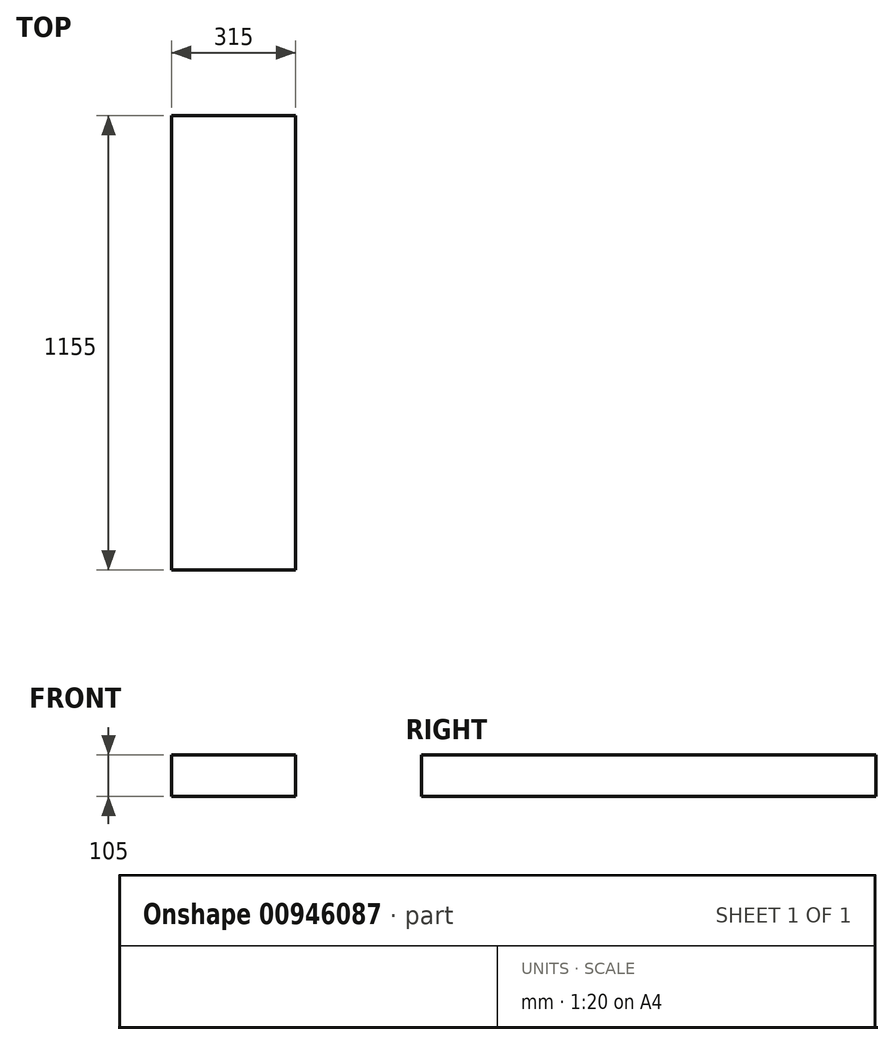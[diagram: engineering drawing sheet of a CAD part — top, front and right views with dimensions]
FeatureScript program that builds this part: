
annotation { "Feature Type Name" : "Feature", "Feature Type Description" : "" }
export const myFeature = defineFeature(function(context is Context, id is Id, definition is map)
    precondition{}
    {
        {
            var Q0;
            Q0=qCreatedBy(makeId("Top.planeOp"),FACE);
            var sketch = newSketch(context, id + "F0", { "sketchPlane" : qUnion([Q0])});
            skLineSegment(sketch, "E0.bottom", {"start": v(-283.8, 1138.94) * mm, "end": v(31.2, 1138.94) * mm});
            skLineSegment(sketch, "E0.top", {"start": v(-283.8, -16.06) * mm, "end": v(31.2, -16.06) * mm});
            skLineSegment(sketch, "E0.left", {"start": v(-283.8, 1138.94) * mm, "end": v(-283.8, -16.06) * mm});
            skLineSegment(sketch, "E0.right", {"start": v(31.2, 1138.94) * mm, "end": v(31.2, -16.06) * mm});
            skSolve(sketch);
        }
        {
            var Q0;
            Q0=qSketchRegion(id+"F0",true);
            extrude(context, id + "F1", {"entities" : qUnion([Q0]), "depth" : 105 * mm, "offsetDistance" : 25 * mm});
        }
    });
